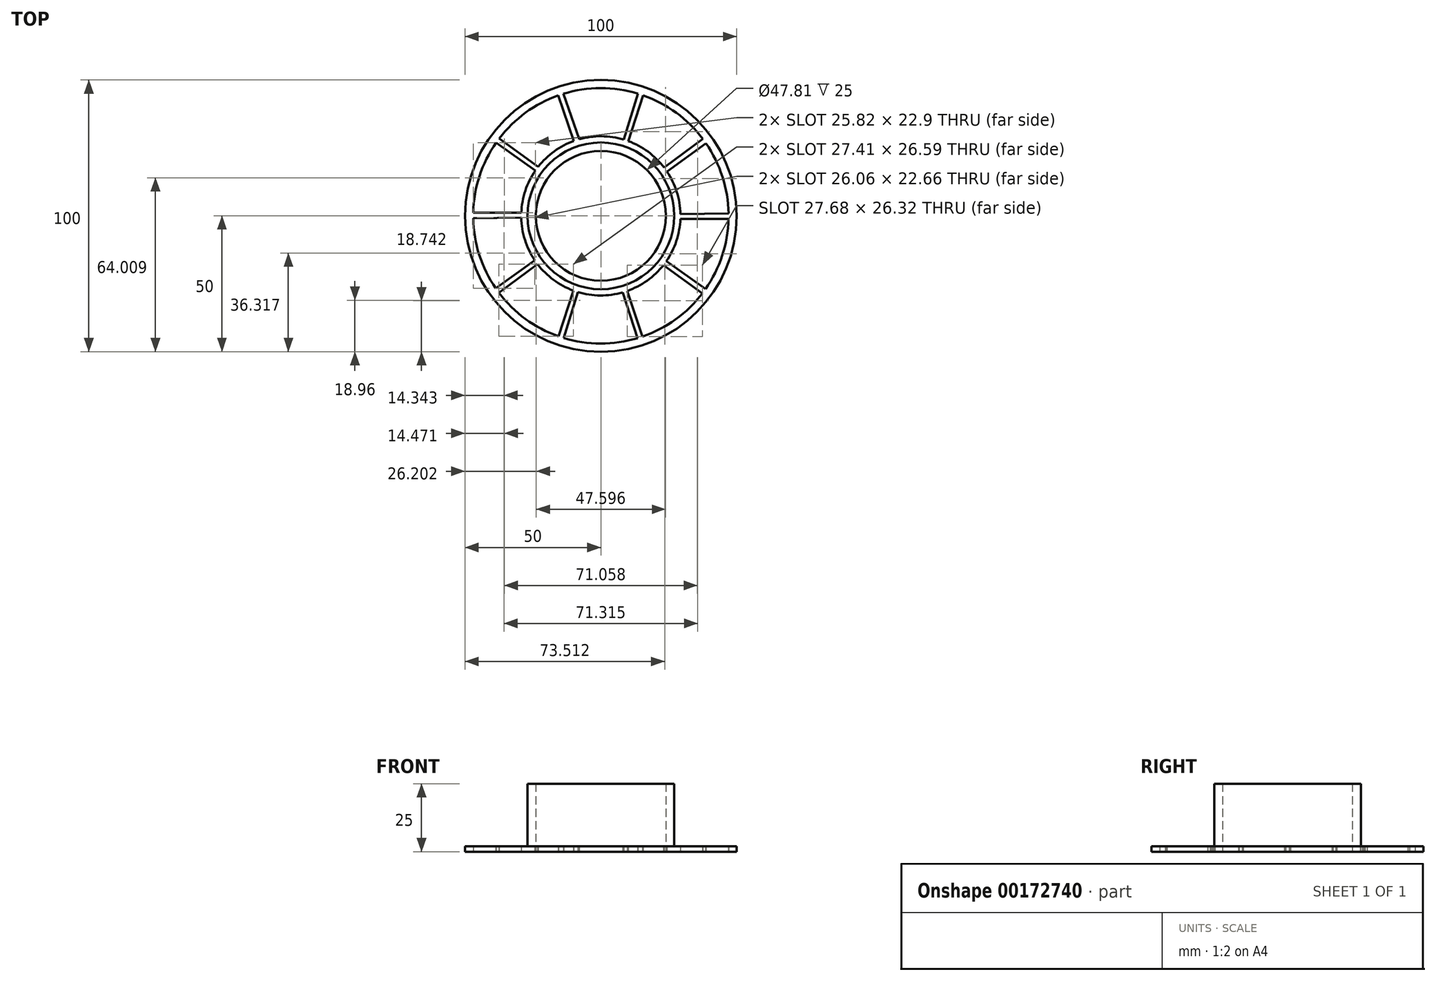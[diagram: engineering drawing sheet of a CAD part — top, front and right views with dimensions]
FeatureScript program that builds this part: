
annotation { "Feature Type Name" : "Feature", "Feature Type Description" : "" }
export const myFeature = defineFeature(function(context is Context, id is Id, definition is map)
    precondition{}
    {
        {
            var Q0;
            Q0=qCreatedBy(makeId("Top.planeOp"),FACE);
            var sketch = newSketch(context, id + "F0", { "sketchPlane" : qUnion([Q0])});
            skCircle(sketch, "E0", {"center": v(0, 0) * mm, "radius": 50 * mm});
            skCircle(sketch, "E1", {"center": v(0, 0) * mm, "radius": 27 * mm});
            skCircle(sketch, "E2", {"center": v(0, 0) * mm, "radius": 47 * mm});
            skCircle(sketch, "E3", {"center": v(0, 0) * mm, "radius": 29.3 * mm});
            skLineSegment(sketch, "E4", {"start": v(-9.91, 27.57) * mm, "end": v(-9.91, 27.57) * mm});
            skLineSegment(sketch, "E5", {"start": v(-9.91, 27.57) * mm, "end": v(-15.75, 44.28) * mm});
            skLineSegment(sketch, "E6", {"start": v(-13.83, 44.91) * mm, "end": v(-7.99, 28.18) * mm});
            skLineSegment(sketch, "E7", {"start": v(8.43, 28.06) * mm, "end": v(13.7, 44.95) * mm});
            skLineSegment(sketch, "E8", {"start": v(10.1, 27.5) * mm, "end": v(15.58, 44.34) * mm});
            skLineSegment(sketch, "E9.2.0", {"start": v(-24.08, 16.69) * mm, "end": v(-38.52, 26.92) * mm});
            skLineSegment(sketch, "E9.2.1", {"start": v(-23.04, 18.1) * mm, "end": v(-37.35, 28.52) * mm});
            skLineSegment(sketch, "E9.3.0", {"start": v(-29.29, -0.65) * mm, "end": v(-46.99, -0.86) * mm});
            skLineSegment(sketch, "E9.3.1", {"start": v(-29.27, 1.1) * mm, "end": v(-46.98, 1.11) * mm});
            skLineSegment(sketch, "E9.4.0", {"start": v(-23.3, -17.74) * mm, "end": v(-37.5, -28.32) * mm});
            skLineSegment(sketch, "E9.4.1", {"start": v(-24.33, -16.32) * mm, "end": v(-38.66, -26.71) * mm});
            skLineSegment(sketch, "E9.5.0", {"start": v(-8.43, -28.06) * mm, "end": v(-13.7, -44.95) * mm});
            skLineSegment(sketch, "E9.5.1", {"start": v(-10.1, -27.5) * mm, "end": v(-15.58, -44.34) * mm});
            skLineSegment(sketch, "E9.6.0", {"start": v(9.67, -27.65) * mm, "end": v(15.34, -44.42) * mm});
            skLineSegment(sketch, "E9.6.1", {"start": v(8, -28.18) * mm, "end": v(13.46, -45.03) * mm});
            skLineSegment(sketch, "E9.7.0", {"start": v(24.08, -16.69) * mm, "end": v(38.52, -26.92) * mm});
            skLineSegment(sketch, "E9.7.1", {"start": v(23.04, -18.1) * mm, "end": v(37.35, -28.52) * mm});
            skLineSegment(sketch, "E9.8.0", {"start": v(29.29, 0.65) * mm, "end": v(46.99, 0.86) * mm});
            skLineSegment(sketch, "E9.8.1", {"start": v(29.27, -1.1) * mm, "end": v(46.98, -1.11) * mm});
            skLineSegment(sketch, "E9.9.0", {"start": v(23.3, 17.74) * mm, "end": v(37.5, 28.32) * mm});
            skLineSegment(sketch, "E9.9.1", {"start": v(24.33, 16.32) * mm, "end": v(38.66, 26.71) * mm});
            skSolve(sketch);
        }
        {
            var Q0;
            Q0 = qSketchRegion(id + "F0", true);
            var Q1;
            Q1=makeQuery(id+"F0.imprint","IMPRINT",FACE,{"disambiguationData":[TD([[makeQuery(id+"F0.imprint","IMPRINT",EDGE,{"derivedFrom":sQuery(id+"F0.wireOp",EDGE,"E1")}),-1.0]])]});
            var Q2;
            {var subQ0=sQuery(id+"F0.wireOp",EDGE,"E5");Q2=makeQuery(id+"F0.imprint","IMPRINT",FACE,{"disambiguationData":[TD([[makeQuery(id+"F0.imprint","IMPRINT",EDGE,{"derivedFrom":subQ0}),-1.0]])]});}
            var Q3;
            {var subQ0=sQuery(id+"F0.wireOp",EDGE,"E9.2.0");Q3=makeQuery(id+"F0.imprint","IMPRINT",FACE,{"disambiguationData":[TD([[makeQuery(id+"F0.imprint","IMPRINT",EDGE,{"derivedFrom":subQ0}),-1.0]])]});}
            var Q4;
            {var subQ0=sQuery(id+"F0.wireOp",EDGE,"E9.3.0");Q4=makeQuery(id+"F0.imprint","IMPRINT",FACE,{"disambiguationData":[TD([[makeQuery(id+"F0.imprint","IMPRINT",EDGE,{"derivedFrom":subQ0}),-1.0]])]});}
            var Q5;
            {var subQ0=sQuery(id+"F0.wireOp",EDGE,"E9.4.0");Q5=makeQuery(id+"F0.imprint","IMPRINT",FACE,{"disambiguationData":[TD([[makeQuery(id+"F0.imprint","IMPRINT",EDGE,{"derivedFrom":subQ0}),-1.0]])]});}
            var Q6;
            {var subQ0=sQuery(id+"F0.wireOp",EDGE,"E9.5.0");Q6=makeQuery(id+"F0.imprint","IMPRINT",FACE,{"disambiguationData":[TD([[makeQuery(id+"F0.imprint","IMPRINT",EDGE,{"derivedFrom":subQ0}),-1.0]])]});}
            var Q7;
            {var subQ0=sQuery(id+"F0.wireOp",EDGE,"E9.6.0");Q7=makeQuery(id+"F0.imprint","IMPRINT",FACE,{"disambiguationData":[TD([[makeQuery(id+"F0.imprint","IMPRINT",EDGE,{"derivedFrom":subQ0}),-1.0]])]});}
            var Q8;
            {var subQ0=sQuery(id+"F0.wireOp",EDGE,"E9.7.0");Q8=makeQuery(id+"F0.imprint","IMPRINT",FACE,{"disambiguationData":[TD([[makeQuery(id+"F0.imprint","IMPRINT",EDGE,{"derivedFrom":subQ0}),-1.0]])]});}
            var Q9;
            {var subQ0=sQuery(id+"F0.wireOp",EDGE,"E9.8.0");Q9=makeQuery(id+"F0.imprint","IMPRINT",FACE,{"disambiguationData":[TD([[makeQuery(id+"F0.imprint","IMPRINT",EDGE,{"derivedFrom":subQ0}),-1.0]])]});}
            var Q10;
            {var subQ0=sQuery(id+"F0.wireOp",EDGE,"E9.9.0");Q10=makeQuery(id+"F0.imprint","IMPRINT",FACE,{"disambiguationData":[TD([[makeQuery(id+"F0.imprint","IMPRINT",EDGE,{"derivedFrom":subQ0}),-1.0]])]});}
            var Q11;
            {var subQ0=sQuery(id+"F0.wireOp",EDGE,"E7");Q11=makeQuery(id+"F0.imprint","IMPRINT",FACE,{"disambiguationData":[TD([[makeQuery(id+"F0.imprint","IMPRINT",EDGE,{"derivedFrom":subQ0}),-1.0]])]});}
            extrude(context, id + "F1", {"entities" : qUnion([Q0, Q1, Q2, Q3, Q4, Q5, Q6, Q7, Q8, Q9, Q10, Q11]), "depth" : 2 * mm});
        }
        {
            var Q0;
            Q0=qCreatedBy(makeId("Top.planeOp"),FACE);
            var sketch = newSketch(context, id + "F2", { "sketchPlane" : qUnion([Q0])});
            skCircle(sketch, "E10", {"center": v(0, 0) * mm, "radius": 27 * mm});
            skCircle(sketch, "E11", {"center": v(0, 0) * mm, "radius": 23.9 * mm});
            skSolve(sketch);
        }
        {
            var Q0;
            Q0=makeQuery(id+"F2.imprint","IMPRINT",FACE,{"disambiguationData":[TD([[makeQuery(id+"F2.imprint","IMPRINT",EDGE,{"derivedFrom":sQuery(id+"F2.wireOp",EDGE,"E10")}),1.0]])]});
            extrude(context, id + "F3", {"entities" : qUnion([Q0]), "operationType" : NewBodyOperationType.ADD, "depth" : 25 * mm});
        }
    });
